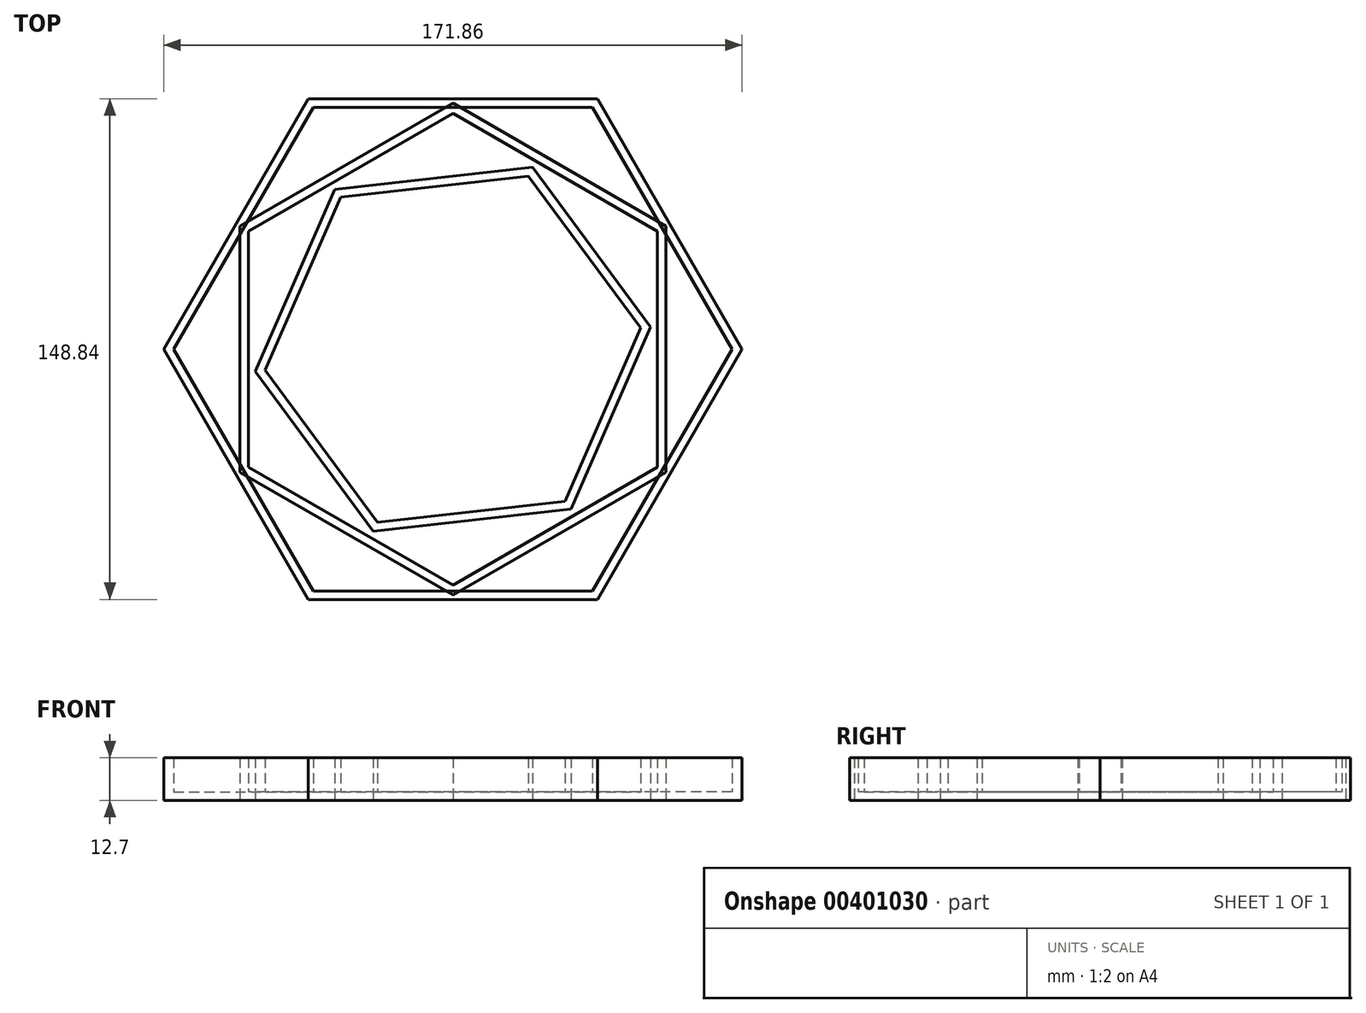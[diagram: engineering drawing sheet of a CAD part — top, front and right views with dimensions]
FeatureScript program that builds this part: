
annotation { "Feature Type Name" : "Feature", "Feature Type Description" : "" }
export const myFeature = defineFeature(function(context is Context, id is Id, definition is map)
    precondition{}
    {
        {
            var Q0;
            Q0=qCreatedBy(makeId("Top.planeOp"),FACE);
            var sketch = newSketch(context, id + "F0", { "sketchPlane" : qUnion([Q0])});
            skCircle(sketch, "E0.cCircle", {"center": v(0, 0) * mm, "radius": 74.42 * mm, "construction": true});
            skLineSegment(sketch, "E0.0", {"start": v(42.96, -74.42) * mm, "end": v(-42.96, -74.42) * mm});
            skLineSegment(sketch, "E0.1", {"start": v(-42.96, -74.42) * mm, "end": v(-85.93, 0) * mm});
            skLineSegment(sketch, "E0.2", {"start": v(-85.93, 0) * mm, "end": v(-42.96, 74.42) * mm});
            skLineSegment(sketch, "E0.3", {"start": v(-42.96, 74.42) * mm, "end": v(42.96, 74.42) * mm});
            skLineSegment(sketch, "E0.4", {"start": v(42.96, 74.42) * mm, "end": v(85.93, 0) * mm});
            skLineSegment(sketch, "E0.5", {"start": v(85.93, 0) * mm, "end": v(42.96, -74.42) * mm});
            skPoint(sketch, "E0.0.midPoint", {"position": v(0, -74.42) * mm});
            skSolve(sketch);
        }
        {
            var Q0;
            Q0=qCreatedBy(makeId("Top.planeOp"),FACE);
            var sketch = newSketch(context, id + "F1", { "sketchPlane" : qUnion([Q0])});
            skCircle(sketch, "E1.cCircle", {"center": v(0, 0) * mm, "radius": 63.29 * mm, "construction": true});
            skLineSegment(sketch, "E1.0", {"start": v(-63.29, -36.54) * mm, "end": v(-63.29, 36.54) * mm});
            skLineSegment(sketch, "E1.1", {"start": v(-63.29, 36.54) * mm, "end": v(0, 73.08) * mm});
            skLineSegment(sketch, "E1.2", {"start": v(0, 73.08) * mm, "end": v(63.29, 36.54) * mm});
            skLineSegment(sketch, "E1.3", {"start": v(63.29, 36.54) * mm, "end": v(63.29, -36.54) * mm});
            skLineSegment(sketch, "E1.4", {"start": v(63.29, -36.54) * mm, "end": v(0, -73.08) * mm});
            skLineSegment(sketch, "E1.5", {"start": v(0, -73.08) * mm, "end": v(-63.29, -36.54) * mm});
            skPoint(sketch, "E1.0.midPoint", {"position": v(-63.29, 0) * mm});
            skSolve(sketch);
        }
        {
            var Q0;
            Q0=makeQuery(id+"F0.imprint","IMPRINT",FACE,{"disambiguationData":[TD([[makeQuery(id+"F0.imprint","IMPRINT",EDGE,{"derivedFrom":sQuery(id+"F0.wireOp",EDGE,"E0.0")}),-1.0]])]});
            var Q1;
            Q1=makeQuery(id+"F1.imprint","IMPRINT",FACE,{"disambiguationData":[TD([[makeQuery(id+"F1.imprint","IMPRINT",EDGE,{"derivedFrom":sQuery(id+"F1.wireOp",EDGE,"E1.0")}),-1.0]])]});
            extrude(context, id + "F2", {"entities" : qUnion([Q0, Q1]), "depth" : 12.7 * mm});
        }
        {
            var Q0;
            Q0=makeQuery(id+"F2.opExtrude","CAP_FACE",FACE,{"disambiguationData":[OSD([sQuery(id+"F0.wireOp",EDGE,"E0.0"),sQuery(id+"F0.wireOp",EDGE,"E0.1"),sQuery(id+"F0.wireOp",EDGE,"E0.2"),sQuery(id+"F0.wireOp",EDGE,"E0.3"),sQuery(id+"F0.wireOp",EDGE,"E0.4"),sQuery(id+"F0.wireOp",EDGE,"E0.5")])],"isStart":false});
            var Q1;
            Q1=makeQuery(id+"F2.opExtrude","CAP_FACE",FACE,{"disambiguationData":[OSD([sQuery(id+"F1.wireOp",EDGE,"E1.0"),sQuery(id+"F1.wireOp",EDGE,"E1.1"),sQuery(id+"F1.wireOp",EDGE,"E1.2"),sQuery(id+"F1.wireOp",EDGE,"E1.3"),sQuery(id+"F1.wireOp",EDGE,"E1.4"),sQuery(id+"F1.wireOp",EDGE,"E1.5")])],"isStart":false});
            shell(context, id + "F3", {"entities" : qUnion([Q0, Q1]), "thickness" : 2.54 * mm});
        }
        {
            var Q0;
            Q0=qCreatedBy(makeId("Top.planeOp"),FACE);
            var sketch = newSketch(context, id + "F4", { "sketchPlane" : qUnion([Q0])});
            skCircle(sketch, "E2", {"center": v(0, 0) * mm, "radius": 59.64 * mm});
            skSolve(sketch);
        }
        {
            var Q0;
            Q0=sQuery(id+"F4.wireOp",EDGE,"E2");
            extrude(context, id + "F5", {"bodyType" : ToolBodyType.SURFACE, "surfaceEntities" : qUnion([Q0]), "depth" : 12.7 * mm});
        }
        {
            var Q0;
            Q0=qCreatedBy(makeId("Top.planeOp"),FACE);
            var sketch = newSketch(context, id + "F6", { "sketchPlane" : qUnion([Q0])});
            skCircle(sketch, "E3.cCircle", {"center": v(0, 0) * mm, "radius": 51.16 * mm, "construction": true});
            skLineSegment(sketch, "E3.0", {"start": v(-35.07, 47.54) * mm, "end": v(23.64, 54.14) * mm});
            skLineSegment(sketch, "E3.1", {"start": v(23.64, 54.14) * mm, "end": v(58.7, 6.6) * mm});
            skLineSegment(sketch, "E3.2", {"start": v(58.7, 6.6) * mm, "end": v(35.07, -47.54) * mm});
            skLineSegment(sketch, "E3.3", {"start": v(35.07, -47.54) * mm, "end": v(-23.64, -54.14) * mm});
            skLineSegment(sketch, "E3.4", {"start": v(-23.64, -54.14) * mm, "end": v(-58.7, -6.6) * mm});
            skLineSegment(sketch, "E3.5", {"start": v(-58.7, -6.6) * mm, "end": v(-35.07, 47.54) * mm});
            skPoint(sketch, "E3.0.midPoint", {"position": v(-5.72, 50.84) * mm});
            skSolve(sketch);
        }
        {
            var Q0;
            Q0 = qSketchRegion(id + "F6", true);
            extrude(context, id + "F7", {"entities" : qUnion([Q0]), "depth" : 12.7 * mm});
        }
        {
            var Q0;
            Q0=makeQuery(id+"F7.opExtrude","CAP_FACE",FACE,{"disambiguationData":[OSD([sQuery(id+"F6.wireOp",EDGE,"E3.0"),sQuery(id+"F6.wireOp",EDGE,"E3.1"),sQuery(id+"F6.wireOp",EDGE,"E3.2"),sQuery(id+"F6.wireOp",EDGE,"E3.3"),sQuery(id+"F6.wireOp",EDGE,"E3.4"),sQuery(id+"F6.wireOp",EDGE,"E3.5")])],"isStart":false});
            shell(context, id + "F8", {"entities" : qUnion([Q0]), "thickness" : 2.54 * mm});
        }
    });
